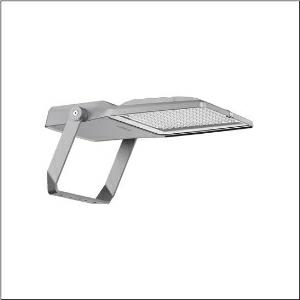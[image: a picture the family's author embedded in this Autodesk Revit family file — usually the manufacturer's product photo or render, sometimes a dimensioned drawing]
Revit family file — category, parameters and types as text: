
# Revit family: floodlight_fl_21_midi___pl64_5xa7786e4e1a_bb08
name_source: partatom
category: Lighting Fixtures
units: mm (PartAtom-declared; Revit-internal decimal feet)

## family parameters
Cut with Voids When Loaded = No
Host = Face
Light Source = No
Part Type = Normal
Room Calculation Point = No
Round Connector Dimension = Use Diameter
Shared = No

## types (1)
- --- (1 x LED, 27140 lm, 212.4 W, 4000K)
    Apparent Load = 212 VA
    CIE Flux Codes = 28 80 98 100 100
    Color Rendering = 70
    Color Temperature = 4000K
    Default Elevation = 1800 mm
    Description = Floodlight FL 21 midi, floodlight, primary light control with lens, of PMMA, primary optical cover: protective disc, of toughened safety glass, transparent, light distribution: PL64, light emission: direct distribution, installation type: surface-mounted, LED, High Power LED, rated luminous flux: 27.140lm, luminous efficacy: 128lm/W, light colour: 740, colour temperature: 4000K, control gear: Smart Interface (Zhaga)D4i, control: overheat protection, constant luminous flux control, time-dependent luminous flux control, flexible luminous flux parameterisation, pre-setting: logarithmic dimming characteristic, with terminal, 6-pole, mains connection: 220..240V, AC, 50/60Hz, start of lifetime: 212W, end of service life: 231W, reduction: 95W, mounting bracket, of diecast aluminium, powder-coated, Siteco® metallic grey (DB 702S), corrosivity category C5 mid according to DIN EN ISO 12944, suitable for swimming pools, chlorine-resistant, sealing non-destructively replaceable, mounting bracket, of steel, galvanised, powder-coated, Siteco® metallic grey (DB 702S), Smart Interface below and above, protection rating (complete): IP66, insulation class (complete): insulation class II (safety insulation), certification: CE, ENEC, VDE, protection symbol: D, impact resistance: IK08, permissible operating ambient temperature: -40..+40°C, permissible operating ambient temperature for outdoor applications: -40..+50°C, standard: DIN EN 12944, LABS conformity tested according to VDMA 24364:2018-05, packaging unit: 1 piece

Light Distribution: PL64
    Height = 76 mm
    Lamp = 1 x LED
    Lamp Light Flux = 27140 lm
    Lamp Power = 212.4 W
    Lamp count = 1
    Length = 657 mm
    Luminous efficacy = 128 lm/W
    Manufacturer = Siteco
    ModVariant = No
    Model = 5XA7786E4E1A
    Number of Poles = 1
    OnlyDefault = Yes
    Power Factor = 1
    Product Name = Floodlight FL 21 midi | PL64
    Product group = floodlight | pylon annexe
    ProductGroupID = 6200
    Protection Class = Protection class II
    Protection Degree = IP 66
    RLX_Detail_Level = 1
    RLX_Emergency_Light_Flux = 0 lm
    RLX_Emergency_Type = 0
    RLX_Emergency_Type_DB = No
    RlxData = <blob elided: 101537 chars, md5=c54d6a27>
    Socket = socket
    Standby Power = 0 W
    System Light Flux = 27140 lm
    System Power = 212 W
    Type Comments = factory setting: luminous flux: 100 % | dim-lin: 254 | 710 mA
    Type Image = l_1006876.jpg
    URL = http://relux.com
    VarID = @adj_089450
    Voltage = 0 V
    Weight = 0.00 kg
    Width = 442 mm

## geometry (parser evidence)
native form markers: Blend x4, Sweep x12
no freeform markers — native parametric forms only
